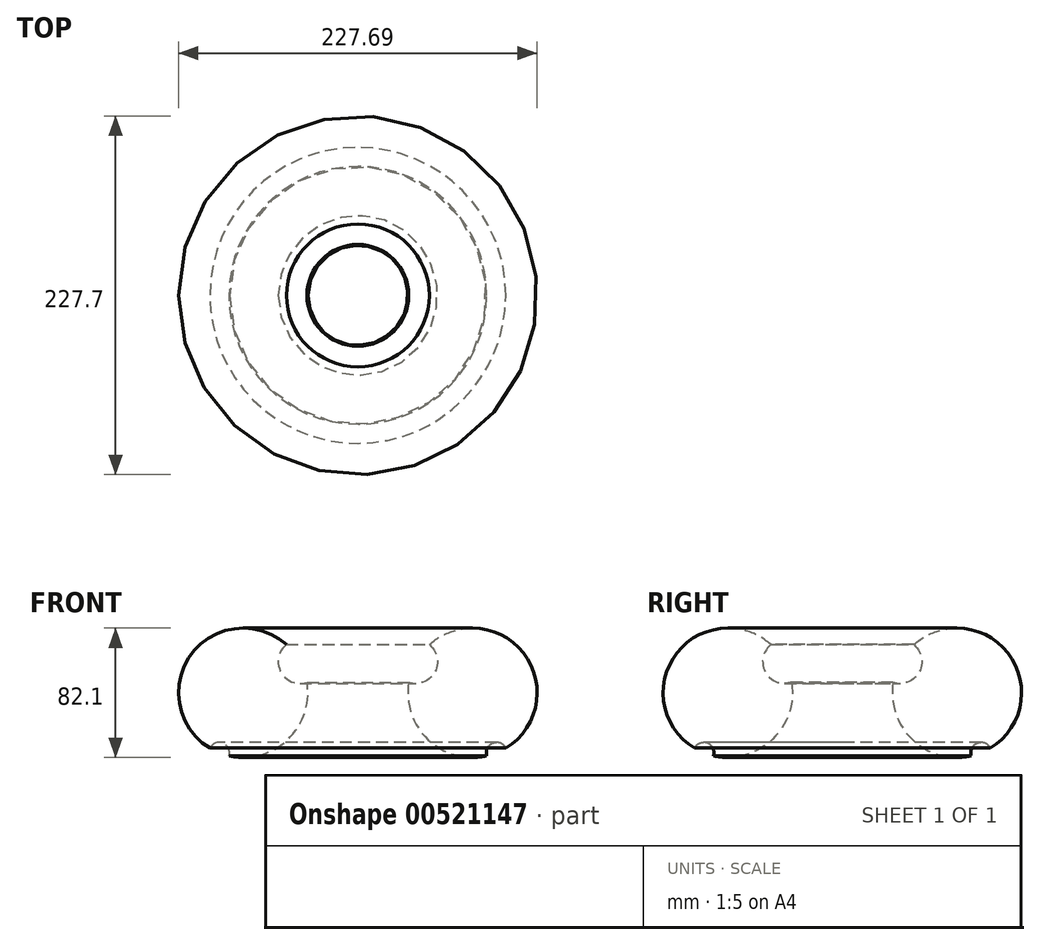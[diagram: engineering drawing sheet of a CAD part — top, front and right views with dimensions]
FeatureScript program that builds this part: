
annotation { "Feature Type Name" : "Feature", "Feature Type Description" : "" }
export const myFeature = defineFeature(function(context is Context, id is Id, definition is map)
    precondition{}
    {
        {
            var Q0;
            Q0=qCreatedBy(makeId("Front.planeOp"),FACE);
            var sketch = newSketch(context, id + "F0", { "sketchPlane" : qUnion([Q0])});
            skArc(sketch, "E0", {"start": v(-40.5, 6.67) * mm, "mid": v(-28.16, -29.87) * mm, "end": v(9.05, -40.04) * mm});
            skArc(sketch, "E1", {"start": v(-40.5, 6.67) * mm, "mid": v(-23.9, 13.09) * mm, "end": v(-27.43, 30.54) * mm});
            skArc(sketch, "E2", {"start": v(21.18, -35.16) * mm, "mid": v(12.86, -32) * mm, "end": v(9.05, -40.04) * mm});
            skArc(sketch, "E3.trimOffspring", {"start": v(21.18, -35.16) * mm, "mid": v(33, 24.42) * mm, "end": v(-27.43, 30.54) * mm});
            skLineSegment(sketch, "E4", {"start": v(-72.8, 0) * mm, "end": v(-72.8, 52.2) * mm});
            skSolve(sketch);
        }
        {
            var Q0;
            Q0 = qSketchRegion(id + "F0", true);
            var Q1;
            Q1=sQuery(id+"F0.wireOp",EDGE,"E4");
            revolve(context, id + "F1", {"entities" : qUnion([Q0]), "axis" : qUnion([Q1]), "revolveType" : RevolveType.FULL});
        }
    });
